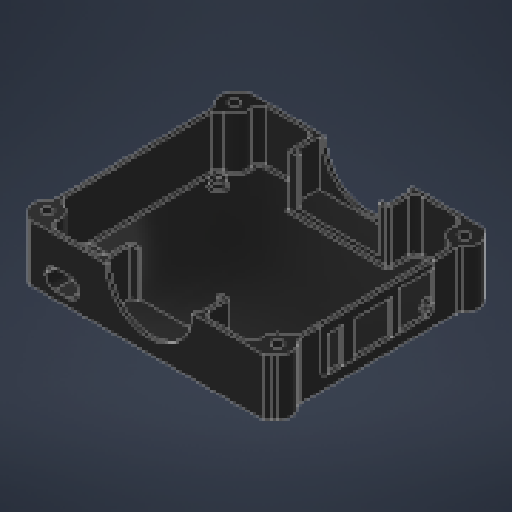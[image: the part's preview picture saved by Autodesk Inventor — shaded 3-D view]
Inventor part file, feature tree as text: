
AUTODESK INVENTOR PART (.ipt)
format: ipt  version: 2023 (Build 270158000, 158)  size: 1,181,184 bytes
history: native  units: in
note: dims shown in document units (in); Inventor stores cm internally (conversion verified against a paired STEP export)
features: sketch x21, extrude x19, reference x14, projected_geometry x11, other x5, plane x3, fillet x3, hole x2
ambient origin geometry x8: Origin, YZ Plane, XZ Plane, XY Plane, X Axis, Y Axis, Z Axis, Center Point
bodies: Solid1 (feature_tree), Solid2 (feature_tree), Solid3 (feature_tree), Solid4 (feature_tree)
feature tree (78):
  plane  "Work Plane1"
  extrude  "Extrusion1"  Depth=0.04in
  extrude  "Extrusion2"  Depth=0.5512in
  extrude  "Extrusion3"  Depth=0.065in
  extrude  "Extrusion4"  TaperAngle=0.0deg  [1 undecoded]
  extrude  "Extrusion5"  Depth=0.7874in TaperAngle=0.0deg
  extrude  "Extrusion6"  Depth=0.0787in TaperAngle=0.0deg
  sketch  "Sketch7"  dims[d16=0.1in d17=0.1181in d18=0.0in]
  plane  "Work Plane2"
  extrude  "Extrusion7"  Depth=0.1181in TaperAngle=0.0deg
  extrude  "Extrusion8"  Depth=0.1181in TaperAngle=0.0deg
  extrude  "Extrusion9"  Depth=0.1181in TaperAngle=0.0deg
  sketch  "Sketch10"  dims[d28=1.7853in d29=0.05in]
  plane  "Work Plane3"
  extrude  "Extrusion10"  Depth=0.05in
  extrude  "Extrusion11"  Depth=0.05in
  extrude  "Extrusion12"  Depth=0.8661in
  hole  "Hole1"  [1 undecoded]
  extrude  "Extrusion13"  Depth=0.1in
  fillet  "Fillet1"  Radius=0.1in
  extrude  "Extrusion14"  Depth=0.063in
  fillet  "Fillet2"  Radius=0.063in
  hole  "Hole2"  [1 undecoded]
  fillet  "Fillet3"  Radius=1.0in
  extrude  "Extrusion15"  Depth=1.7323in
  extrude  "Extrusion16"  Depth=1.0in TaperAngle=0.0deg
  extrude  "Extrusion17"  Depth=0.1in
  extrude  "Extrusion18"  Depth=0.063in
  extrude  "Extrusion19"  Depth=0.1in
  sketch  "Sketch1"  dims[d0=0.04in d1=0.04in]
  reference  "Reference1"
  reference  "Reference2"
  sketch  "Sketch2"  dims[d2=0.5512in d3=0.5512in]
  projected_geometry  "Projected Loop1"
  sketch  "Sketch3"  dims[d5=0.065in d6=0.065in]
  sketch  "Sketch4"  dims[d7=0.065in d8=0.0in]
  reference  "Reference3"
  reference  "Reference4"
  reference  "Reference5"
  reference  "Reference6"
  sketch  "Sketch5"  dims[d9=0.065in d10=0.7874in d11=0.0in]
  reference  "Reference7"
  reference  "Reference8"
  reference  "Reference9"
  sketch  "Sketch6"  dims[d12=0.1969in d13=0.0in d14=0.0787in d15=0.0in]
  reference  "Reference10"
  reference  "Reference11"
  sketch  "Sketch8"  dims[d19=0.6378in d22=0.1181in d23=0.0in]
  projected_geometry  "Projected Loop2"
  sketch  "Sketch9"  dims[d24=0.05in d25=0.1181in d26=0.0in]
  sketch  "Sketch11"  dims[d30=0.15in d31=0.05in]
  sketch  "Sketch12"  dims[d32=1.7323in d33=0.8661in]
  sketch  "Sketch13"  dims[d34=0.4843in d35=1.0in d36=0.0in]
  sketch  "Sketch14"  dims[d45=1.0in d46=0.0in d47=0.1in d48=0.1in]
  projected_geometry  "Projected Loop3"
  projected_geometry  "Projected Loop4"
  sketch  "Sketch15"  dims[d49=0.063in d50=0.063in d51=0.063in]
  sketch  "Sketch17"  dims[d52=0.063in d53=1.4961in d54=1.0in d55=0.0in]
  sketch  "Sketch18"  dims[d56=0.4724in d57=1.7323in]
  projected_geometry  "Projected Loop5"
  sketch  "Sketch19"  dims[d58=0.8661in d59=1.0in d60=0.0in]
  projected_geometry  "Projected Loop6"
  sketch  "Sketch20"  dims[d62=0.063in d63=0.1in]
  projected_geometry  "Projected Loop7"
  projected_geometry  "Projected Loop8"
  projected_geometry  "Projected Loop9"
  projected_geometry  "Projected Loop10"
  sketch  "Sketch21"  dims[d64=0.063in d65=0.063in]
  projected_geometry  "Projected Loop11"
  sketch  "Sketch22"  dims[d66=0.063in d67=0.1in d68=1.0in d69=0.0in d70=1.4961in d71=1.0in d72=0.0in d73=0.0793in d74=0.197in d75=0.173in d76=0.079in d77=0.5635in d78=1.0in d79=0.8108in d80=0.0394in d81=0.625in d82=0.0in d83=0.125in d84=3.25in d85=4.0in d86=0.4724in d87=0.1969in d88=0.0in d89=0.125in d90=0.177in d91=0.75in d92=0.313in d93=0.75in d94=0.5635in d95=1.0in d96=0.8108in d97=0.0312in d98=0.0079in d99=0.0in d100=0.0079in d101=0.0in d102=0.0079in d103=0.0in d104=0.0079in d105=0.0in d106=0.1875in d107=1.0in d108=0.0in]
  reference  "Reference12"
  reference  "Reference13"
  reference  "Reference14"
  other  "OrangePICover.iam"
  other  "OPi5_pcb_asm-0809:1"
  other  "orangepicover-002:1"
  other  "OPi5_pcb_asm-0809:2"
  other  "Assembly10"
note: 3 required parameter values undecoded (feature->parameter linkage not recoverable at this tier; creation-order binding heuristic only, values carry confidence <= 0.55)
